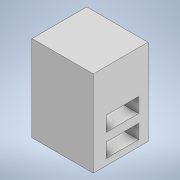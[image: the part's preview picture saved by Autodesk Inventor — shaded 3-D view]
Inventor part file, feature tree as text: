
AUTODESK INVENTOR PART (.ipt)
format: ipt  version: 2021 (Build 250183000, 183)  size: 108,544 bytes
history: native  units: in
note: dims shown in document units (in); Inventor stores cm internally (conversion verified against a paired STEP export)
features: extrude x3, sketch x3
ambient origin geometry x8: Origin, YZ Plane, XZ Plane, XY Plane, X Axis, Y Axis, Z Axis, Center Point
bodies: Solid1 (feature_tree)
feature tree (6):
  extrude  "Extrusion1"  Depth=0.4in TaperAngle=0.0deg
  extrude  "Extrusion2"  [1 undecoded]
  extrude  "Extrusion3"  [1 undecoded]
  sketch  "Sketch1"  dims[d0=0.7in d1=0.0in d2=0.4in d3=0.0in]
  sketch  "Sketch2"  dims[d4=1.0in d5=0.0in]
  sketch  "Sketch3"
note: 2 required parameter values undecoded (feature->parameter linkage not recoverable at this tier; creation-order binding heuristic only, values carry confidence <= 0.55)
